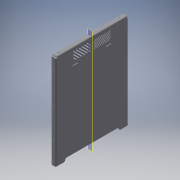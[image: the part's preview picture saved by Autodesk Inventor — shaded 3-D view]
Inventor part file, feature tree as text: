
AUTODESK INVENTOR PART (.ipt)
format: ipt  version: 2018 (Build 220112000, 112)  size: 479,232 bytes
history: native  units: mm
features: other x13, reference x11, sketch x8, extrude x6, plane x1
ambient origin geometry x8: Origin, YZ Plane, XZ Plane, XY Plane, X Axis, Y Axis, Z Axis, Center Point
bodies: Volumenkörper1 (feature_tree)
feature tree (39):
  other  "Fläche1"
  other  "Lasche1"
  extrude  "Extrusion1"  Depth=343.0mm
  extrude  "Extrusion2"  Depth=10.0mm
  plane  "Arbeitsebene1"
  extrude  "Extrusion3"  Depth=5.0mm
  extrude  "Extrusion4"  Depth=15.0mm
  extrude  "Extrusion5"  Depth=2.0mm
  extrude  "Extrusion6"  Depth=2.0mm
  sketch  "Skizze1"  dims[d0=263.0mm d1=343.0mm]
  other  "Grobblech1"
  sketch  "Skizze2"  dims[d2=10.0mm d3=34.0mm]
  other  "Grobblech2"
  other  "Biegung1"
  other  "Ecke1"
  sketch  "Skizze3"  dims[d4=5.0mm d5=5.0mm]
  reference  "Referenz1"
  reference  "Referenz2"
  reference  "Referenz3"
  sketch  "Skizze4"  dims[d6=4.3mm d7=15.0mm]
  reference  "Referenz4"
  reference  "Referenz5"
  reference  "Referenz6"
  sketch  "Skizze6"  dims[d8=29.0mm d9=2.0mm]
  reference  "Referenz9"
  reference  "Referenz10"
  sketch  "Skizze7"  dims[d10=2.0mm d11=1.0mm]
  reference  "Referenz11"
  reference  "Referenz12"
  sketch  "Skizze8"  dims[d12=4.0mm]
  sketch  "Skizze9"  dims[d13=2.0mm d14=15.0mm d15=90.0deg d16=2.0mm d17=8.0mm d18=2.0mm d19=2.0mm d20=10.0mm d21=0.0mm d22=10.0mm d23=0.0mm d24=20.0mm d25=50.0mm d26=0.15mm d27=10.0mm d28=0.0mm d29=10.0mm d30=0.0mm d31=10.0mm d32=0.0mm d33=7.0mm d34=3.5mm d35=0.0mm d36=3.0mm d37=60.0mm d38=30.0mm d39=3.0mm d40=3.0mm d41=3.0mm d42=70.0mm d44=10.0mm d45=10.0mm d47=10.0mm d49=40.0mm d51=10.0mm d52=10.0mm d54=10.0mm d56=70.0mm d58=10.0mm d59=10.0mm d61=10.0mm d63=40.0mm d65=10.0mm d66=10.0mm d68=10.0mm d70=2.5mm d71=2.5mm d72=2.5mm d73=2.5mm d74=2.5mm d75=2.5mm d76=2.5mm d77=2.5mm d78=10.0mm d79=0.0mm d80=3.3mm d81=3.3mm d82=3.3mm]
  reference  "Referenz13"
  parser-record x1  (decoder bookkeeping rows leaked as tree rows — omitted from the tree; the rows remain in map.json)
  other  "Montiert.iam"
  other  "Front:1"
  other  "Deckel:1"
  other  "Gegenhalter:1"
  other  "Brenner:1"
  other  "Definition1"
note: 1 file-system path scrubbed to <path> (originals preserved in map.json)
